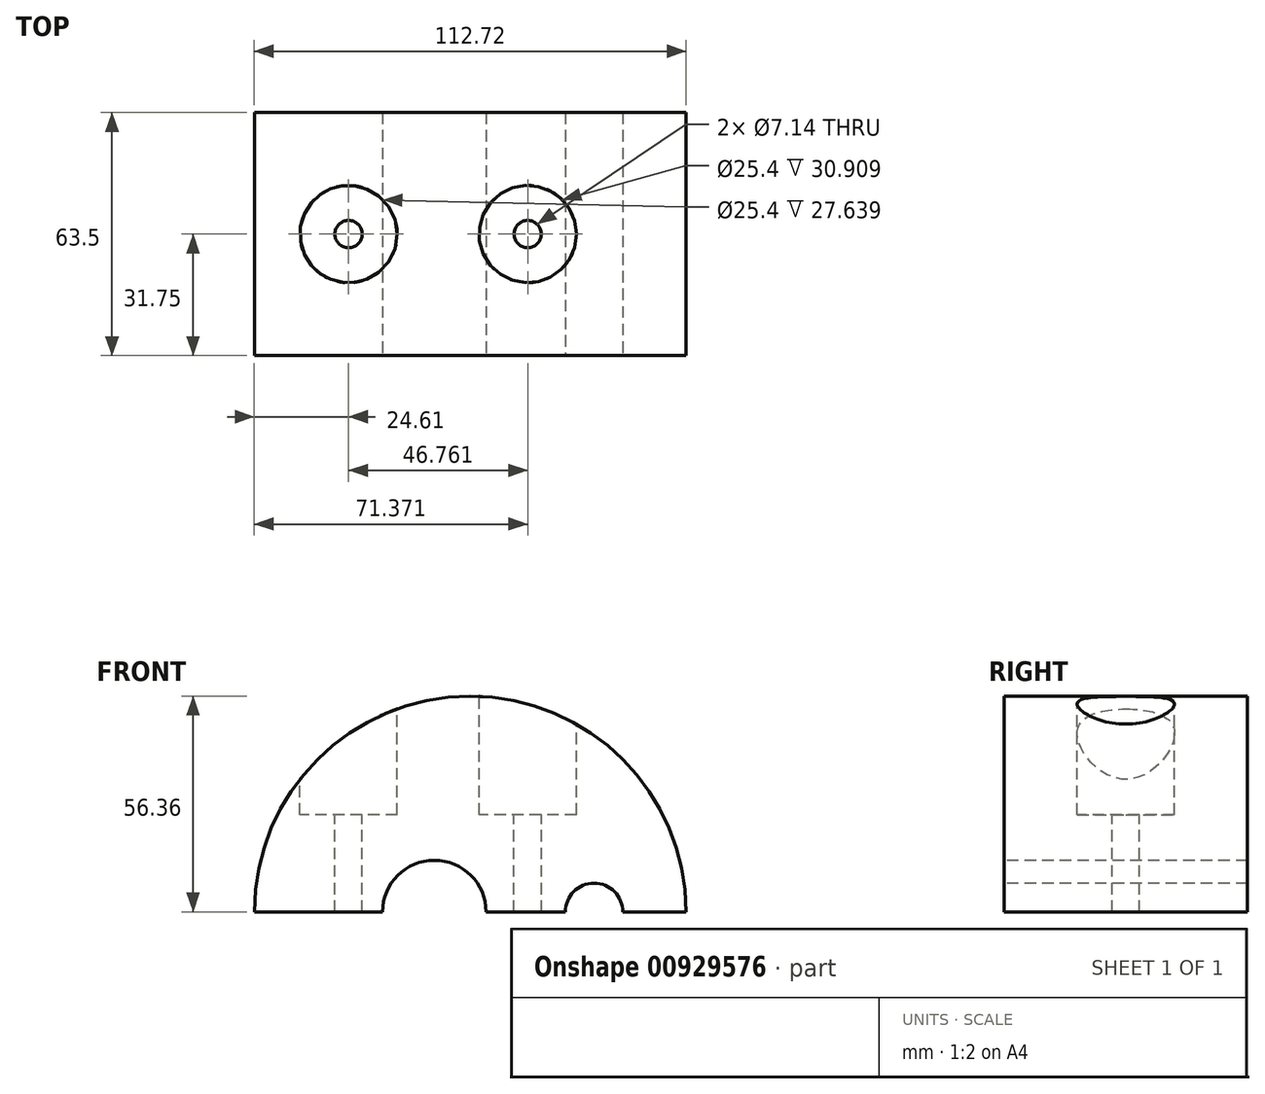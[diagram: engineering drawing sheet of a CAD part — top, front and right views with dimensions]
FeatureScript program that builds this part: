
annotation { "Feature Type Name" : "Feature", "Feature Type Description" : "" }
export const myFeature = defineFeature(function(context is Context, id is Id, definition is map)
    precondition{}
    {
        {
            var Q0;
            Q0=qCreatedBy(makeId("Front.planeOp"),FACE);
            var sketch = newSketch(context, id + "F0", { "sketchPlane" : qUnion([Q0])});
            skCircle(sketch, "E0", {"center": v(0, 0) * mm, "radius": 56.36 * mm});
            skSolve(sketch);
        }
        {
            var Q0;
            Q0=makeQuery(id+"F0.imprint","IMPRINT",FACE,{"disambiguationData":[TD([[makeQuery(id+"F0.imprint","IMPRINT",EDGE,{"derivedFrom":sQuery(id+"F0.wireOp",EDGE,"E0")}),1.0]])]});
            extrude(context, id + "F1", {"entities" : qUnion([Q0]), "oppositeDirection" : true, "depth" : 63.5 * mm, "offsetDistance" : 25.4 * mm, "symmetric" : true});
        }
        {
            var Q0;
            Q0=makeQuery(id+"F1.opExtrude","CAP_FACE",FACE,{"disambiguationData":[OSD([sQuery(id+"F0.wireOp",EDGE,"E0")])],"isStart":true});
            var sketch = newSketch(context, id + "F2", { "sketchPlane" : qUnion([Q0])});
            skCircle(sketch, "E1", {"center": v(-9.36, 0) * mm, "radius": 13.5 * mm});
            skCircle(sketch, "E2", {"center": v(32.36, 0) * mm, "radius": 7.5 * mm});
            skSolve(sketch);
        }
        {
            var Q0;
            Q0=makeQuery(id+"F2.imprint","IMPRINT",FACE,{"disambiguationData":[TD([[makeQuery(id+"F2.imprint","IMPRINT",EDGE,{"derivedFrom":sQuery(id+"F2.wireOp",EDGE,"E1")}),1.0]])]});
            var Q1;
            Q1=makeQuery(id+"F2.imprint","IMPRINT",FACE,{"disambiguationData":[TD([[makeQuery(id+"F2.imprint","IMPRINT",EDGE,{"derivedFrom":sQuery(id+"F2.wireOp",EDGE,"E2")}),1.0]])]});
            extrude(context, id + "F3", {"entities" : qUnion([Q0, Q1]), "operationType" : NewBodyOperationType.REMOVE, "endBound" : BoundingType.THROUGH_ALL, "oppositeDirection" : true, "depth" : 63.5 * mm, "offsetDistance" : 25.4 * mm});
        }
        {
            var Q0;
            Q0=qCreatedBy(makeId("Top.planeOp"),FACE);
            var sketch = newSketch(context, id + "F4", { "sketchPlane" : qUnion([Q0])});
            skCircle(sketch, "E3", {"center": v(-31.75, 0) * mm, "radius": 12.7 * mm});
            skCircle(sketch, "E4", {"center": v(15.01, 0) * mm, "radius": 12.7 * mm});
            skSolve(sketch);
        }
        {
            var Q0;
            Q0=makeQuery(id+"F1.opExtrude","CAP_FACE",FACE,{"disambiguationData":[OSD([sQuery(id+"F0.wireOp",EDGE,"E0")])],"isStart":false});
            var sketch = newSketch(context, id + "F5", { "sketchPlane" : qUnion([Q0])});
            skLineSegment(sketch, "E5", {"start": v(61.45, 0) * mm, "end": v(61.45, 25.4) * mm});
            skLineSegment(sketch, "E6", {"start": v(64.15, 0) * mm, "end": v(64.15, -25.4) * mm});
            skLineSegment(sketch, "E7", {"start": v(61.45, 25.4) * mm, "end": v(-50.3, 25.4) * mm});
            skLineSegment(sketch, "E8", {"start": v(64.15, -25.4) * mm, "end": v(-50.3, -25.4) * mm});
            skSolve(sketch);
        }
        {
            var Q0;
            Q0=qCreatedBy(makeId("Top.planeOp"),FACE);
            var sketch = newSketch(context, id + "F6", { "sketchPlane" : qUnion([Q0])});
            skCircle(sketch, "E9", {"center": v(-31.75, 0) * mm, "radius": 12.7 * mm});
            skCircle(sketch, "E10", {"center": v(15.01, 0) * mm, "radius": 12.7 * mm});
            skSolve(sketch);
        }
        {
            var Q0;
            Q0=qCreatedBy(makeId("Top.planeOp"),FACE);
            var sketch = newSketch(context, id + "F7", { "sketchPlane" : qUnion([Q0])});
            skCircle(sketch, "E11", {"center": v(-34.3, 0) * mm, "radius": 3.57 * mm});
            skCircle(sketch, "E12", {"center": v(15.01, 0) * mm, "radius": 3.5 * mm});
            skSolve(sketch);
        }
        {
            var Q0;
            Q0 = qSketchRegion(id + "F7", true);
            extrude(context, id + "F8", {"entities" : qUnion([Q0]), "operationType" : NewBodyOperationType.REMOVE, "endBound" : BoundingType.THROUGH_ALL, "oppositeDirection" : true, "depth" : 25.4 * mm, "offsetDistance" : 25.4 * mm, "hasSecondDirection" : true, "secondDirectionBound" : BoundingType.THROUGH_ALL, "secondDirectionOppositeDirection" : false, "secondDirectionDepth" : 25.4 * mm});
        }
        {
            var Q0;
            Q0 = qSketchRegion(id + "F4", true);
            extrude(context, id + "F9", {"entities" : qUnion([Q0]), "operationType" : NewBodyOperationType.REMOVE, "endBound" : BoundingType.THROUGH_ALL, "oppositeDirection" : true, "depth" : 25.4 * mm, "offsetDistance" : 25.4 * mm, "hasSecondDirection" : true, "secondDirectionBound" : BoundingType.THROUGH_ALL, "secondDirectionOppositeDirection" : false, "secondDirectionDepth" : 25.4 * mm});
        }
        {
            var Q0;
            Q0 = qSketchRegion(id + "F6", true);
            extrude(context, id + "F10", {"entities" : qUnion([Q0]), "operationType" : NewBodyOperationType.ADD, "depth" : 25.4 * mm, "offsetDistance" : 25.4 * mm, "hasSecondDirection" : true, "secondDirectionOppositeDirection" : true, "secondDirectionDepth" : 25.4 * mm});
        }
        {
            var Q0;
            Q0=qCreatedBy(makeId("Top.planeOp"),FACE);
            var sketch = newSketch(context, id + "F11", { "sketchPlane" : qUnion([Q0])});
            skCircle(sketch, "E13", {"center": v(-31.75, 0) * mm, "radius": 3.57 * mm});
            skCircle(sketch, "E14", {"center": v(15.01, 0) * mm, "radius": 3.57 * mm});
            skSolve(sketch);
        }
        {
            var Q0;
            Q0 = qSketchRegion(id + "F11", true);
            extrude(context, id + "F12", {"entities" : qUnion([Q0]), "operationType" : NewBodyOperationType.REMOVE, "endBound" : BoundingType.THROUGH_ALL, "oppositeDirection" : true, "depth" : 25.4 * mm, "offsetDistance" : 25.4 * mm, "hasSecondDirection" : true, "secondDirectionBound" : BoundingType.THROUGH_ALL, "secondDirectionOppositeDirection" : false, "secondDirectionDepth" : 25.4 * mm});
        }
        {
            var Q0;
            Q0=makeQuery(id+"F5.imprint","IMPRINT",FACE,{"disambiguationData":[TD([[makeQuery(id+"F5.imprint","IMPRINT",EDGE,{"derivedFrom":makeQuery(id+"F3.boolean.opBoolean","INTERSECT",EDGE,{"derivedFrom":[makeQuery(id+"F1.opExtrude","CAP_FACE",FACE,{"disambiguationData":[OSD([sQuery(id+"F0.wireOp",EDGE,"E0")])],"isStart":false}),makeQuery(id+"F3.opExtrude","SWEPT_FACE",FACE,{"disambiguationData":[OSD([sQuery(id+"F2.wireOp",EDGE,"E1")])]})]})}),-1.0]])]});
            var Q1;
            Q1=makeQuery(id+"F5.imprint","IMPRINT",FACE,{"disambiguationData":[TD([[makeQuery(id+"F5.imprint","IMPRINT",EDGE,{"derivedFrom":makeQuery(id+"F3.boolean.opBoolean","INTERSECT",EDGE,{"derivedFrom":[makeQuery(id+"F1.opExtrude","CAP_FACE",FACE,{"disambiguationData":[OSD([sQuery(id+"F0.wireOp",EDGE,"E0")])],"isStart":false}),makeQuery(id+"F3.opExtrude","SWEPT_FACE",FACE,{"disambiguationData":[OSD([sQuery(id+"F2.wireOp",EDGE,"E2")])]})]})}),-1.0]])]});
            extrude(context, id + "F13", {"entities" : qUnion([Q0, Q1]), "operationType" : NewBodyOperationType.REMOVE, "endBound" : BoundingType.THROUGH_ALL, "oppositeDirection" : true, "depth" : 25.4 * mm, "offsetDistance" : 25.4 * mm, "hasSecondDirection" : true, "secondDirectionBound" : BoundingType.THROUGH_ALL, "secondDirectionOppositeDirection" : false, "secondDirectionDepth" : 25.4 * mm});
        }
        {
            var Q0;
            Q0=qCreatedBy(makeId("Front.planeOp"),FACE);
            var sketch = newSketch(context, id + "F14", { "sketchPlane" : qUnion([Q0])});
            skLineSegment(sketch, "E15.bottom", {"start": v(-72.17, 0) * mm, "end": v(81.2, 0) * mm});
            skLineSegment(sketch, "E15.top", {"start": v(-72.17, -61.11) * mm, "end": v(81.2, -61.11) * mm});
            skLineSegment(sketch, "E15.left", {"start": v(-72.17, 0) * mm, "end": v(-72.17, -61.11) * mm});
            skLineSegment(sketch, "E15.right", {"start": v(81.2, 0) * mm, "end": v(81.2, -61.11) * mm});
            skSolve(sketch);
        }
        {
            var Q0;
            Q0=makeQuery(id+"F14.imprint","IMPRINT",FACE,{"disambiguationData":[TD([[makeQuery(id+"F14.imprint","IMPRINT",EDGE,{"derivedFrom":sQuery(id+"F14.wireOp",EDGE,"E15.bottom")}),-1.0]])]});
            extrude(context, id + "F15", {"entities" : qUnion([Q0]), "operationType" : NewBodyOperationType.REMOVE, "endBound" : BoundingType.THROUGH_ALL, "depth" : 25.4 * mm, "offsetDistance" : 25.4 * mm, "hasSecondDirection" : true, "secondDirectionBound" : BoundingType.THROUGH_ALL, "secondDirectionOppositeDirection" : true, "secondDirectionDepth" : 25.4 * mm});
        }
    });
